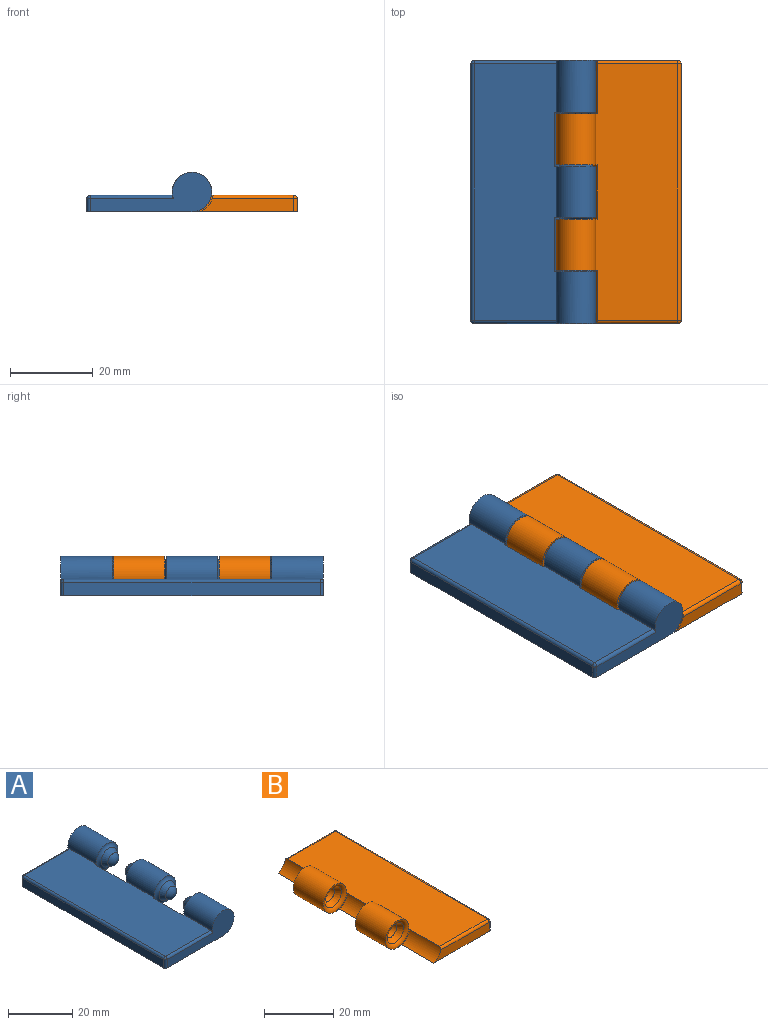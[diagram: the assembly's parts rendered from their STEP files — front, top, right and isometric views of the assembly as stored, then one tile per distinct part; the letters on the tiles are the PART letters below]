
ASSEMBLY  parts=2 mates=1
PART A: 33 faces, bbox 30.6x63.5x10.3 mm
  f0: cylinder r=4.76mm len=12.3mm, axis (0,-1,0), area 285.9mm2, adj f4,f6,f17,f23
  f1: cylinder r=5.16mm len=13.1mm, axis (0,-1,0), area 69mm2, adj f2,f3,f4,f6
  f2: plane 5.1x3.97mm, normal (0,1,0), area 2.2mm2, adj f1,f4,f6,f17
  f3: plane 5.1x3.97mm, normal (0,-1,0), area 2.2mm2, adj f1,f4,f6,f20
  f4: plane 63.5x25.4mm, normal (0,0,-1), area 1560.7mm2, adj f0,f1,f2,f3,f5,f7,f8,f9
  f5: cylinder r=4.76mm len=12.5mm, axis (0,-1,0), area 290.7mm2, adj f4,f6,f9,f20,f27
  f6: plane 61.91x19.91mm, normal (0,0,1), area 1222.2mm2, adj f0,f1,f2,f3,f5,f7,f11,f12
  f7: cylinder r=4.76mm len=12.5mm, axis (0,-1,0), area 290.7mm2, adj f4,f6,f10,f14,f28
  f8: plane 61.91x3.18mm, normal (-1,0,0), area 196.6mm2, adj f4,f26,f29,f32
  f9: plane 29.37x9.53mm, normal (0,1,0), area 139mm2, adj f4,f5,f26,f27
  f10: plane 29.37x9.53mm, normal (0,-1,0), area 139mm2, adj f4,f7,f28,f29
  f11: cylinder r=5.16mm len=13.1mm, axis (0,-1,0), area 69mm2, adj f4,f6,f12,f13
  f12: plane 5.1x3.97mm, normal (0,-1,0), area 2.2mm2, adj f4,f6,f11,f23
  f13: plane 5.1x3.97mm, normal (0,1,0), area 2.2mm2, adj f4,f6,f11,f14
  f14: torus R=4.76mm, axis (0,-1,0), area 41.8mm2, adj f7,f13,f15
  f15: cone r=2.33mm half-angle=30deg, axis (0,-1,0), area 37.9mm2, adj f14,f16
  f16: sphere r=2.69mm, area 22.8mm2, adj f15
  f17: torus R=4.76mm, axis (0,-1,0), area 41.8mm2, adj f0,f2,f18
  f18: cone r=2.33mm half-angle=30deg, axis (0,-1,0), area 37.9mm2, adj f17,f19
  f19: sphere r=2.69mm, area 22.8mm2, adj f18
  f20: torus R=4.76mm, axis (0,1,0), area 41.8mm2, adj f3,f5,f21
  f21: cone r=2.33mm half-angle=30deg, axis (0,1,0), area 37.9mm2, adj f20,f22
  f22: sphere r=2.69mm, area 22.8mm2, adj f21
  f23: torus R=4.76mm, axis (0,1,0), area 41.8mm2, adj f0,f12,f24
  f24: cone r=2.33mm half-angle=30deg, axis (0,1,0), area 37.9mm2, adj f23,f25
  f25: sphere r=2.69mm, area 22.8mm2, adj f24
  f26: cylinder r=0.79mm len=3.18mm, axis (0,0,1), area 4mm2, adj f4,f8,f9,f30
  f27: cylinder r=0.79mm len=20.12mm, axis (1,0,0), area 24.9mm2, adj f5,f6,f9,f30
  f28: cylinder r=0.79mm len=20.12mm, axis (-1,0,0), area 24.9mm2, adj f6,f7,f10,f31
  f29: cylinder r=0.79mm len=3.18mm, axis (0,0,-1), area 4mm2, adj f4,f8,f10,f31
  f30: sphere r=0.79mm, area 1mm2, adj f26,f27,f32
  f31: sphere r=0.79mm, area 1mm2, adj f28,f29,f32
  f32: cylinder r=0.79mm len=61.91mm, axis (0,-1,0), area 77.2mm2, adj f6,f8,f30,f31
PART B: 33 faces, bbox 31.8x63.5x12.7 mm
  f0: plane 5.1x3.97mm, normal (0,1,0), area 2.2mm2, adj f6,f7,f11,f23
  f1: plane 5.1x3.97mm, normal (0,1,0), area 2.2mm2, adj f6,f7,f12,f20
  f2: plane 5.1x3.97mm, normal (0,-1,0), area 2.2mm2, adj f6,f7,f11,f17
  f3: plane 5.1x3.97mm, normal (0,-1,0), area 2.2mm2, adj f6,f7,f13,f14
  f4: cylinder r=4.76mm len=12.3mm, axis (0,-1,0), area 285.9mm2, adj f6,f7,f14,f23
  f5: cylinder r=4.76mm len=12.3mm, axis (0,-1,0), area 285.9mm2, adj f6,f7,f17,f20
  f6: plane 63.5x25.4mm, normal (0,0,-1), area 1535.4mm2, adj f0,f1,f2,f3,f4,f5,f8,f9
  f7: plane 61.91x19.91mm, normal (0,0,1), area 1217.7mm2, adj f0,f1,f2,f3,f4,f5,f11,f12
  f8: plane 61.91x3.18mm, normal (1,0,0), area 196.6mm2, adj f6,f27,f28,f32
  f9: plane 22.62x3.18mm, normal (0,1,0), area 65.8mm2, adj f6,f12,f26,f27
  f10: plane 22.62x3.18mm, normal (0,-1,0), area 65.8mm2, adj f6,f13,f28,f29
  f11: cylinder r=5.16mm len=13.1mm, axis (0,-1,0), area 69mm2, adj f0,f2,f6,f7
  f12: cylinder r=5.16mm len=12.9mm, axis (0,-1,0), area 67.8mm2, adj f1,f6,f7,f9,f26
  f13: cylinder r=5.16mm len=12.9mm, axis (0,-1,0), area 67.8mm2, adj f3,f6,f7,f10,f29
  f14: torus R=4.76mm, axis (0,1,0), area 41.8mm2, adj f3,f4,f15
  f15: cone r=2.33mm half-angle=30deg, axis (0,-1,0), area 37.9mm2, adj f14,f16
  f16: sphere r=2.69mm, area 22.8mm2, adj f15
  f17: torus R=4.76mm, axis (0,1,0), area 41.8mm2, adj f2,f5,f18
  f18: cone r=2.33mm half-angle=30deg, axis (0,-1,0), area 37.9mm2, adj f17,f19
  f19: sphere r=2.69mm, area 22.8mm2, adj f18
  f20: torus R=4.76mm, axis (0,-1,0), area 41.8mm2, adj f1,f5,f21
  f21: cone r=2.33mm half-angle=30deg, axis (0,1,0), area 37.9mm2, adj f20,f22
  f22: sphere r=2.69mm, area 22.8mm2, adj f21
  f23: torus R=4.76mm, axis (0,-1,0), area 41.8mm2, adj f0,f4,f24
  f24: cone r=2.33mm half-angle=30deg, axis (0,1,0), area 37.9mm2, adj f23,f25
  f25: sphere r=2.69mm, area 22.8mm2, adj f24
  f26: cylinder r=0.79mm len=19.7mm, axis (1,0,0), area 24.4mm2, adj f7,f9,f12,f30
  f27: cylinder r=0.79mm len=3.18mm, axis (0,0,-1), area 4mm2, adj f6,f8,f9,f30
  f28: cylinder r=0.79mm len=3.18mm, axis (0,0,1), area 4mm2, adj f6,f8,f10,f31
  f29: cylinder r=0.79mm len=19.7mm, axis (-1,0,0), area 24.4mm2, adj f7,f10,f13,f31
  f30: sphere r=0.79mm, area 1mm2, adj f26,f27,f32
  f31: sphere r=0.79mm, area 1mm2, adj f28,f29,f32
  f32: cylinder r=0.79mm len=61.91mm, axis (0,-1,0), area 77.2mm2, adj f7,f8,f30,f31
PLACE A t=(0,-31.75,0)mm
PLACE B rot(axis=(0,-1,0),0deg) t=(0,-31.75,0)mm
MATE revolute B.f24 <-> A.f24  axis (0,-1,0) through (0,-31.75,4.76)mm
